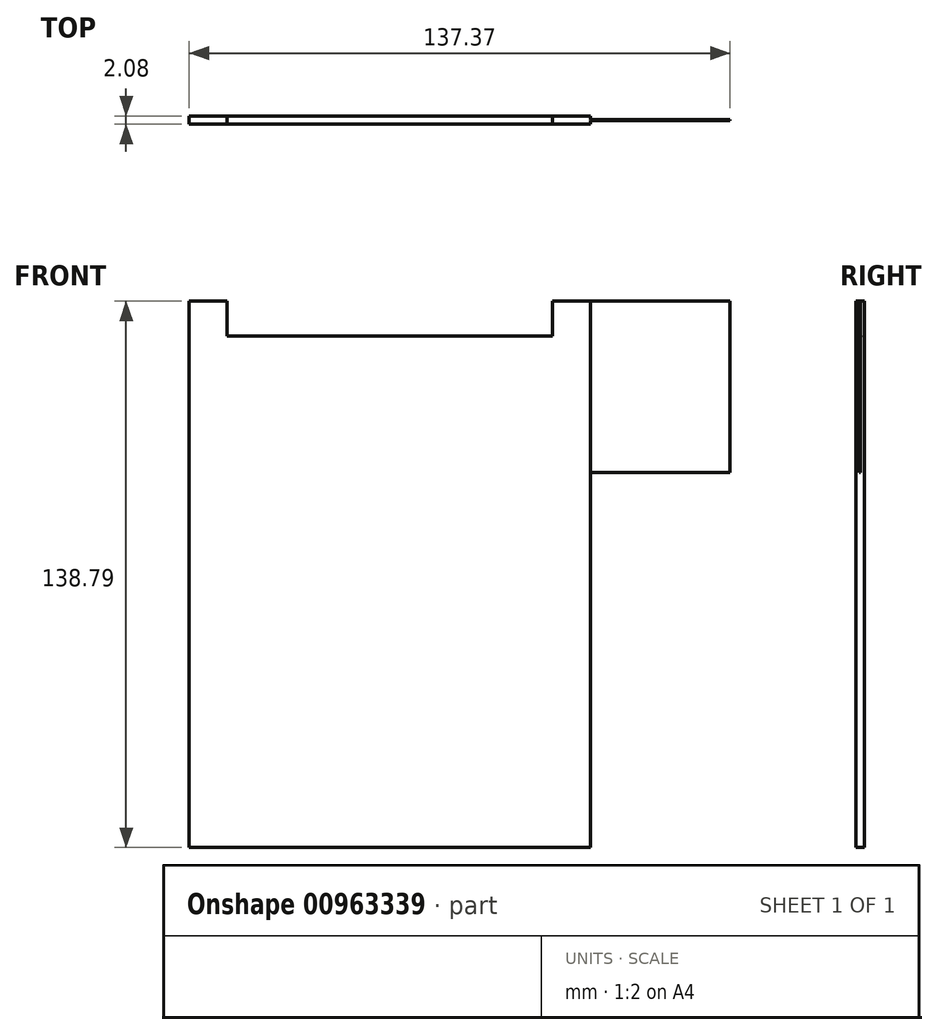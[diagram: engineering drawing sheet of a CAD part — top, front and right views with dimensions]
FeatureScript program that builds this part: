
annotation { "Feature Type Name" : "Feature", "Feature Type Description" : "" }
export const myFeature = defineFeature(function(context is Context, id is Id, definition is map)
    precondition{}
    {
        {
            var Q0;
            Q0=qCreatedBy(makeId("Front.planeOp"),FACE);
            var sketch = newSketch(context, id + "F0", { "sketchPlane" : qUnion([Q0])});
            skLineSegment(sketch, "E0.bottom", {"start": v(-50.95, 138.79) * mm, "end": v(50.95, 138.79) * mm});
            skLineSegment(sketch, "E0.top", {"start": v(-50.95, 0) * mm, "end": v(50.95, 0) * mm});
            skLineSegment(sketch, "E0.left", {"start": v(-50.95, 138.79) * mm, "end": v(-50.95, 0) * mm});
            skLineSegment(sketch, "E0.right", {"start": v(50.95, 138.79) * mm, "end": v(50.95, 0) * mm});
            skLineSegment(sketch, "E1.bottom", {"start": v(50.95, 138.79) * mm, "end": v(86.42, 138.79) * mm});
            skLineSegment(sketch, "E1.top", {"start": v(50.95, 95.32) * mm, "end": v(86.42, 95.32) * mm});
            skLineSegment(sketch, "E1.left", {"start": v(50.95, 138.79) * mm, "end": v(50.95, 95.32) * mm});
            skLineSegment(sketch, "E1.right", {"start": v(86.42, 138.79) * mm, "end": v(86.42, 95.32) * mm});
            skLineSegment(sketch, "E2.bottom", {"start": v(-41.35, 147.6) * mm, "end": v(41.35, 147.6) * mm});
            skLineSegment(sketch, "E2.top", {"start": v(-41.35, 129.98) * mm, "end": v(41.35, 129.98) * mm});
            skLineSegment(sketch, "E2.left", {"start": v(-41.35, 147.6) * mm, "end": v(-41.35, 129.98) * mm});
            skLineSegment(sketch, "E2.right", {"start": v(41.35, 147.6) * mm, "end": v(41.35, 129.98) * mm});
            skPoint(sketch, "E2.middle", {"position": v(0, 138.79) * mm});
            skSolve(sketch);
        }
        {
            var Q0;
            Q0=makeQuery(id+"F0.imprint","IMPRINT",FACE,{"disambiguationData":[TD([[makeQuery(id+"F0.imprint","IMPRINT",EDGE,{"derivedFrom":sQuery(id+"F0.wireOp",EDGE,"E1.bottom")}),-1.0]])]});
            extrude(context, id + "F1", {"entities" : qUnion([Q0]), "endBound" : BoundingType.SYMMETRIC, "depth" : .25 * mm, "offsetDistance" : 25 * mm});
        }
        {
            var Q0;
            Q0=makeQuery(id+"F0.imprint","IMPRINT",FACE,{"disambiguationData":[TD([[makeQuery(id+"F0.imprint","IMPRINT",EDGE,{"derivedFrom":sQuery(id+"F0.wireOp",EDGE,"E0.bottom")}),-1.0]])]});
            extrude(context, id + "F2", {"entities" : qUnion([Q0]), "operationType" : NewBodyOperationType.ADD, "endBound" : BoundingType.SYMMETRIC, "depth" : 2.09 * mm, "offsetDistance" : 25 * mm});
        }
    });
